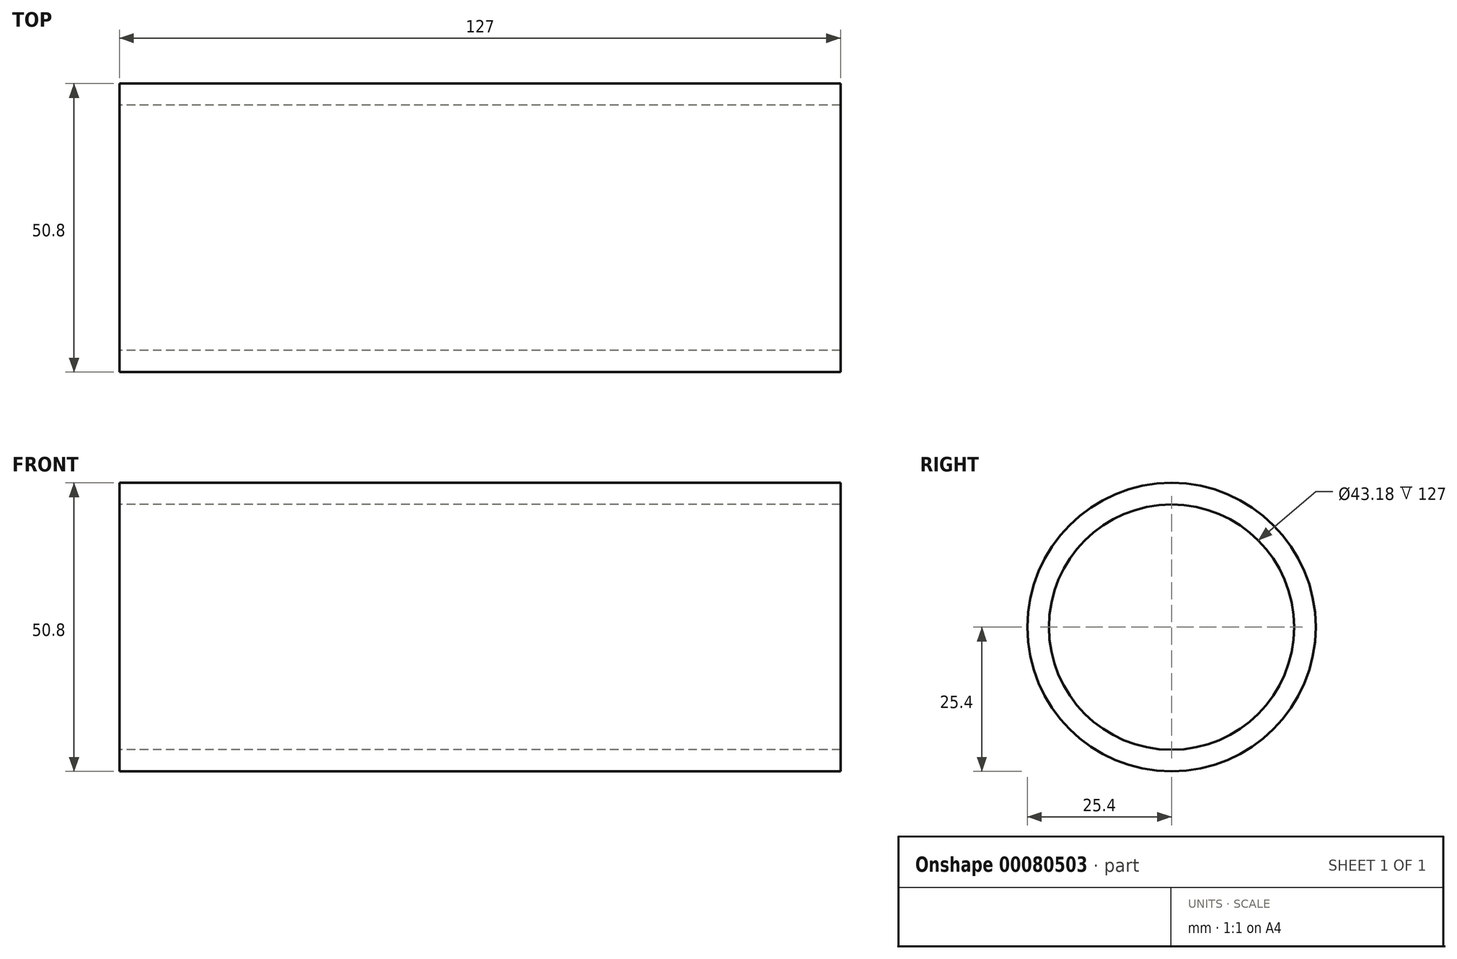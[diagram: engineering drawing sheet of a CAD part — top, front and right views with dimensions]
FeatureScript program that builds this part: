
annotation { "Feature Type Name" : "Feature", "Feature Type Description" : "" }
export const myFeature = defineFeature(function(context is Context, id is Id, definition is map)
    precondition{}
    {
        {
            var Q0;
            Q0=qCreatedBy(makeId("Right.planeOp"),FACE);
            var sketch = newSketch(context, id + "F0", { "sketchPlane" : qUnion([Q0])});
            skCircle(sketch, "E0", {"center": v(0, 0) * mm, "radius": 25.4 * mm});
            skCircle(sketch, "E1", {"center": v(0, 0) * mm, "radius": 21.59 * mm});
            skSolve(sketch);
        }
        {
            var Q0;
            Q0=makeQuery(id+"F0.imprint","IMPRINT",FACE,{"disambiguationData":[TD([[makeQuery(id+"F0.imprint","IMPRINT",EDGE,{"derivedFrom":sQuery(id+"F0.wireOp",EDGE,"E0")}),1.0]])]});
            extrude(context, id + "F1", {"entities" : qUnion([Q0]), "depth" : 127 * mm});
        }
    });
